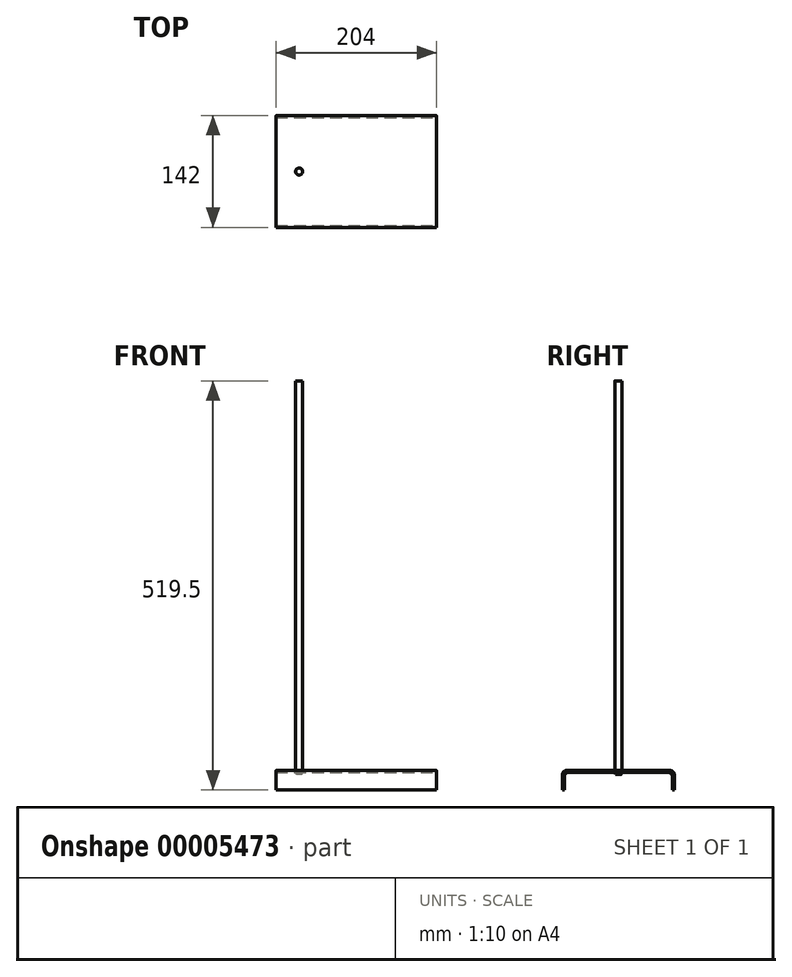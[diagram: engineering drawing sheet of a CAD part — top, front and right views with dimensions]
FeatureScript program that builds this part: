
annotation { "Feature Type Name" : "Feature", "Feature Type Description" : "" }
export const myFeature = defineFeature(function(context is Context, id is Id, definition is map)
    precondition{}
    {
        {
            var Q0;
            Q0=qCreatedBy(makeId("Top.planeOp"),FACE);
            var sketch = newSketch(context, id + "F0", { "sketchPlane" : qUnion([Q0])});
            skLineSegment(sketch, "E0.bottom", {"start": v(-29.5, -71) * mm, "end": v(174.5, -71) * mm});
            skLineSegment(sketch, "E0.top", {"start": v(-29.5, 71) * mm, "end": v(174.5, 71) * mm});
            skLineSegment(sketch, "E0.left", {"start": v(-29.5, -71) * mm, "end": v(-29.5, 71) * mm});
            skLineSegment(sketch, "E0.right", {"start": v(174.5, -71) * mm, "end": v(174.5, 71) * mm});
            skLineSegment(sketch, "E1", {"start": v(0, 71) * mm, "end": v(0, -71) * mm, "construction": true});
            skCircle(sketch, "E2", {"center": v(0, 0) * mm, "radius": 4.5 * mm});
            skCircle(sketch, "E3", {"center": v(0, 0) * mm, "radius": 3.5 * mm});
            skSolve(sketch);
        }
        {
            var Q0;
            Q0=makeQuery(id+"F0.imprint","IMPRINT",FACE,{"disambiguationData":[TD([[makeQuery(id+"F0.imprint","IMPRINT",EDGE,{"derivedFrom":sQuery(id+"F0.wireOp",EDGE,"E0.bottom")}),1.0]])]});
            var Q1;
            Q1=makeQuery(id+"F0.imprint","IMPRINT",FACE,{"disambiguationData":[TD([[makeQuery(id+"F0.imprint","IMPRINT",EDGE,{"derivedFrom":sQuery(id+"F0.wireOp",EDGE,"E2")}),1.0]])]});
            var Q2;
            Q2=makeQuery(id+"F0.imprint","IMPRINT",FACE,{"disambiguationData":[TD([[makeQuery(id+"F0.imprint","IMPRINT",EDGE,{"derivedFrom":sQuery(id+"F0.wireOp",EDGE,"E3")}),1.0]])]});
            extrude(context, id + "F1", {"entities" : qUnion([Q0, Q1, Q2]), "oppositeDirection" : true, "depth" : 24.5 * mm});
        }
        {
            var Q0;
            Q0=makeQuery(id+"F0.imprint","IMPRINT",FACE,{"disambiguationData":[TD([[makeQuery(id+"F0.imprint","IMPRINT",EDGE,{"derivedFrom":sQuery(id+"F0.wireOp",EDGE,"E3")}),1.0]])]});
            var Q1;
            Q1=makeQuery(id+"F0.imprint","IMPRINT",FACE,{"disambiguationData":[TD([[makeQuery(id+"F0.imprint","IMPRINT",EDGE,{"derivedFrom":sQuery(id+"F0.wireOp",EDGE,"E2")}),1.0]])]});
            extrude(context, id + "F2", {"entities" : qUnion([Q0, Q1]), "depth" : 495 * mm});
        }
        {
            var Q0;
            Q0=makeQuery(id+"F1.opExtrude","SWEPT_FACE",FACE,{"disambiguationData":[OSD([sQuery(id+"F0.wireOp",EDGE,"E0.left")])]});
            var Q1;
            Q1=makeQuery(id+"F1.opExtrude","SWEPT_FACE",FACE,{"disambiguationData":[OSD([sQuery(id+"F0.wireOp",EDGE,"E0.right")])]});
            var Q2;
            Q2=makeQuery(id+"F1.opExtrude","CAP_FACE",FACE,{"disambiguationData":[OSD([sQuery(id+"F0.wireOp",EDGE,"E0.bottom"),sQuery(id+"F0.wireOp",EDGE,"E0.top"),sQuery(id+"F0.wireOp",EDGE,"E0.left"),sQuery(id+"F0.wireOp",EDGE,"E0.right"),sQuery(id+"F0.wireOp",EDGE,"E3")])],"isStart":false});
            shell(context, id + "F3", {"entities" : qUnion([Q0, Q1, Q2]), "thickness" : 2.5 * mm});
        }
        {
            var Q0;
            Q0=makeQuery(id+"F0.imprint","IMPRINT",FACE,{"disambiguationData":[TD([[makeQuery(id+"F0.imprint","IMPRINT",EDGE,{"derivedFrom":sQuery(id+"F0.wireOp",EDGE,"E3")}),1.0]])]});
            extrude(context, id + "F4", {"entities" : qUnion([Q0]), "operationType" : NewBodyOperationType.REMOVE, "endBound" : BoundingType.THROUGH_ALL, "oppositeDirection" : true, "depth" : 25 * mm});
        }
        {
            var Q0;
            Q0=makeQuery(id+"F0.imprint","IMPRINT",FACE,{"disambiguationData":[TD([[makeQuery(id+"F0.imprint","IMPRINT",EDGE,{"derivedFrom":sQuery(id+"F0.wireOp",EDGE,"E3")}),1.0]])]});
            extrude(context, id + "F5", {"entities" : qUnion([Q0]), "operationType" : NewBodyOperationType.ADD, "oppositeDirection" : true, "depth" : 5 * mm});
        }
        {
            var Q0;
            Q0=makeQuery(id+"F1.opExtrude","CAP_EDGE",EDGE,{"disambiguationData":[OSD([sQuery(id+"F0.wireOp",EDGE,"E0.top")])],"isStart":true});
            var Q1;
            {var subQ0=sQuery(id+"F0.wireOp",EDGE,"E0.top");Q1=makeQuery(id+"F3.opShell","OFFSET_EDGE",EDGE,{"disambiguationData":[OSD([subQ0]),TDD([makeQuery(id+"F1.opExtrude","CAP_EDGE",EDGE,{"disambiguationData":[OSD([subQ0])],"isStart":true})])]});}
            var Q2;
            Q2=makeQuery(id+"F1.opExtrude","CAP_EDGE",EDGE,{"disambiguationData":[OSD([sQuery(id+"F0.wireOp",EDGE,"E0.bottom")])],"isStart":true});
            var Q3;
            {var subQ0=sQuery(id+"F0.wireOp",EDGE,"E0.bottom");Q3=makeQuery(id+"F3.opShell","OFFSET_EDGE",EDGE,{"disambiguationData":[OSD([subQ0]),TDD([makeQuery(id+"F1.opExtrude","CAP_EDGE",EDGE,{"disambiguationData":[OSD([subQ0])],"isStart":true})])]});}
            fillet(context, id + "F6", {"entities" : qUnion([Q0, Q1, Q2, Q3]), "radius" : 5 * mm, "tangentPropagation" : true, "allowEdgeOverflow" : false});
        }
    });
